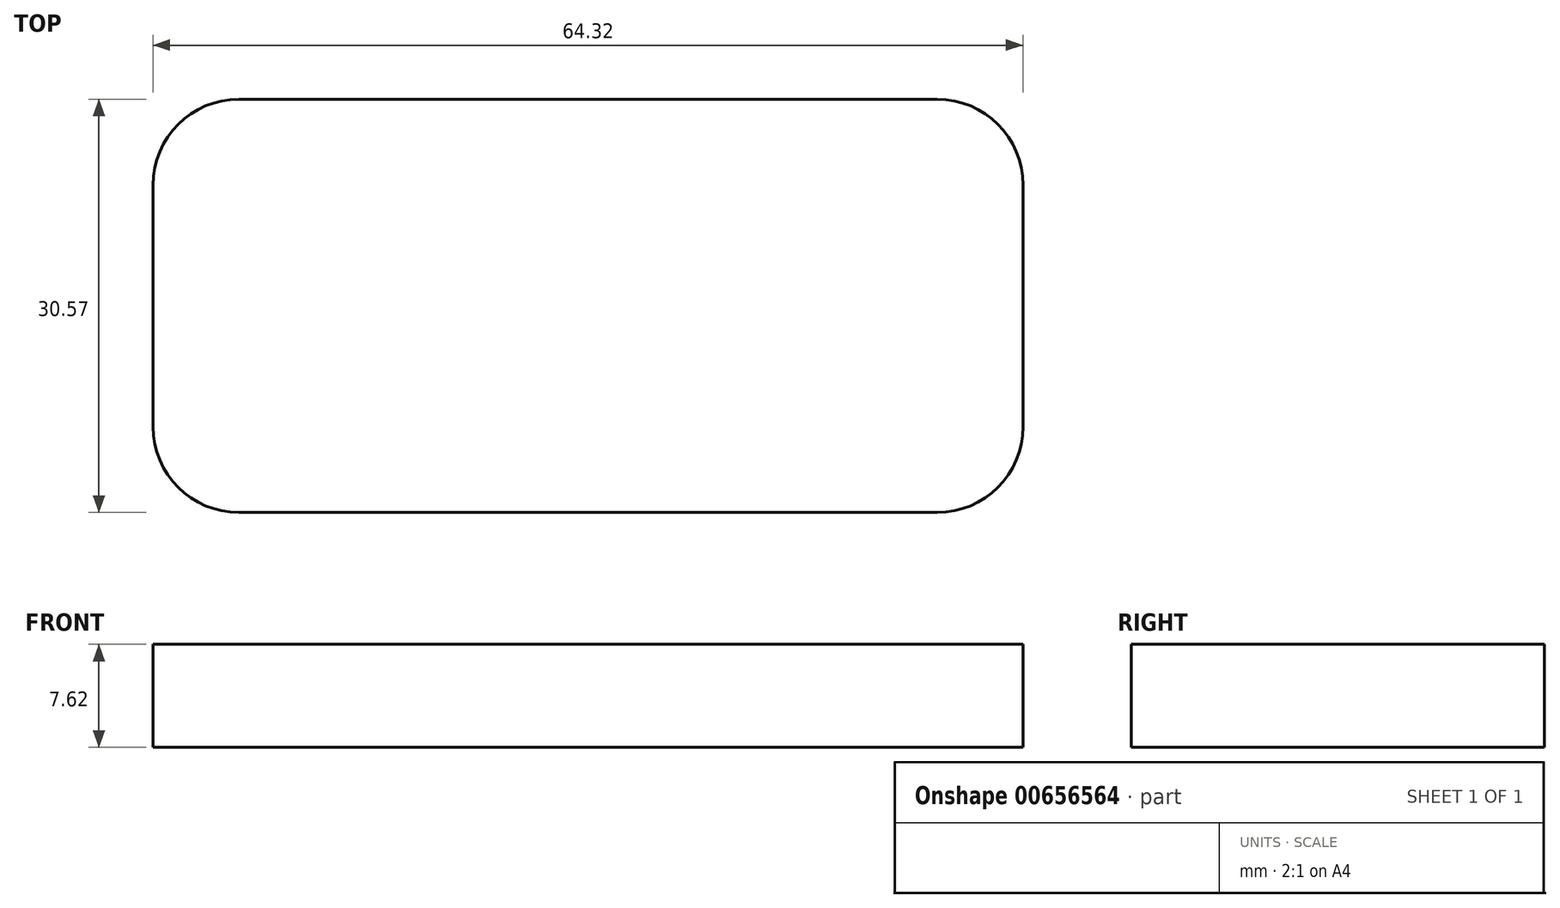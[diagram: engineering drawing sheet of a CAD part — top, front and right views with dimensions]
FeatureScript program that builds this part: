
annotation { "Feature Type Name" : "Feature", "Feature Type Description" : "" }
export const myFeature = defineFeature(function(context is Context, id is Id, definition is map)
    precondition{}
    {
        {
            var Q0;
            Q0=qCreatedBy(makeId("Top.planeOp"),FACE);
            var sketch = newSketch(context, id + "F0", { "sketchPlane" : qUnion([Q0])});
            skLineSegment(sketch, "E0.bottom", {"start": v(-32.08, 0) * mm, "end": v(19.54, 0) * mm});
            skLineSegment(sketch, "E0.top", {"start": v(-32.08, 30.57) * mm, "end": v(19.54, 30.57) * mm});
            skLineSegment(sketch, "E0.left", {"start": v(-38.43, 6.35) * mm, "end": v(-38.43, 24.22) * mm});
            skLineSegment(sketch, "E0.right", {"start": v(25.9, 6.35) * mm, "end": v(25.9, 24.22) * mm});
            skPoint(sketch, "E1.visualSharp", {"position": v(-38.43, 30.57) * mm});
            skArc(sketch, "E1.filletArc", {"start": v(-32.08, 30.57) * mm, "mid": v(-36.57, 28.7) * mm, "end": v(-38.43, 24.22) * mm});
            skPoint(sketch, "E2.visualSharp", {"position": v(-38.43, 0) * mm});
            skArc(sketch, "E2.filletArc", {"start": v(-38.43, 6.35) * mm, "mid": v(-36.57, 1.86) * mm, "end": v(-32.08, 0) * mm});
            skPoint(sketch, "E3.visualSharp", {"position": v(25.9, 0) * mm});
            skArc(sketch, "E3.filletArc", {"start": v(19.54, 0) * mm, "mid": v(24.03, 1.86) * mm, "end": v(25.9, 6.35) * mm});
            skPoint(sketch, "E4.visualSharp", {"position": v(25.9, 30.57) * mm});
            skArc(sketch, "E4.filletArc", {"start": v(25.9, 24.22) * mm, "mid": v(24.03, 28.7) * mm, "end": v(19.54, 30.57) * mm});
            skArc(sketch, "E5.0", {"start": v(-44.78, 6.35) * mm, "mid": v(-41.06, -2.63) * mm, "end": v(-32.08, -6.35) * mm});
            skSolve(sketch);
        }
        {
            var Q0;
            Q0=makeQuery(id+"F0.imprint","IMPRINT",FACE,{"disambiguationData":[TD([[makeQuery(id+"F0.imprint","IMPRINT",EDGE,{"derivedFrom":sQuery(id+"F0.wireOp",EDGE,"E0.bottom")}),1.0]])]});
            extrude(context, id + "F1", {"entities" : qUnion([Q0]), "depth" : 7.62 * mm, "offsetDistance" : 25.4 * mm});
        }
    });
